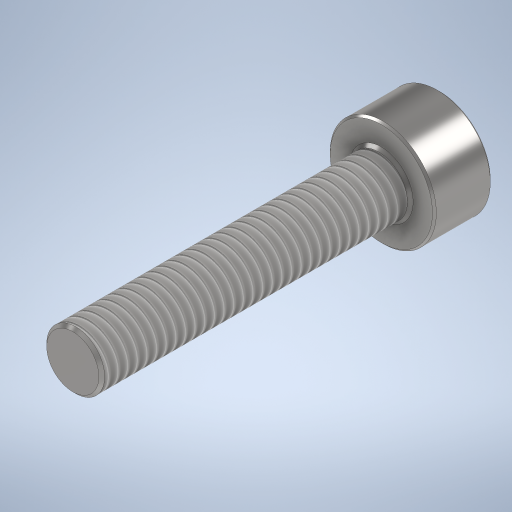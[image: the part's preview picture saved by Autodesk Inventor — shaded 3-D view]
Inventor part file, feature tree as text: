
AUTODESK INVENTOR PART (.ipt)
format: ipt  version: 2024 (Build 280153000, 153)  size: 331,264 bytes
history: native  units: mm
features: extrude x3, chamfer x3, sketch x2, thread x1, hole x1
ambient origin geometry x8: Origin, YZ Plane, XZ Plane, XY Plane, X Axis, Y Axis, Z Axis, Center Point
bodies: Solid1 (feature_tree)
feature tree (10):
  sketch  "Sketch1"  dims[d0=5.5mm d1=3.0mm]
  extrude  "Extrusion1"  Depth=3.0mm
  extrude  "Extrusion2"  Depth=1.5mm TaperAngle=0.0deg
  thread  "Thread1"  [1 undecoded]
  chamfer  "Chamfer1"  Distance=2.5mm
  sketch  "Sketch2"  dims[d2=16.0mm d3=0.0mm d4=3.0mm d5=0.0mm d6=16.0mm d7=0.0mm d8=0.1mm d9=2.0mm d10=45.0deg d11=2.4mm d12=2.5mm d15=0.35mm d16=2.0mm d17=45.0deg d18=3.0mm d19=0.0mm d20=0.15mm d21=2.0mm d22=45.0deg d23=2.4mm d24=6.0mm d25=4.0mm d26=2.0mm d27=90.0deg d28=1.5mm d29=150.0deg]
  hole  "Hole1"  [1 undecoded]
  chamfer  "Chamfer2"  Distance=3.0mm
  extrude  "Extrusion4"  Depth=1.5mm TaperAngle=45.0deg
  chamfer  "Chamfer3"  Distance=2.4mm
note: 2 required parameter values undecoded (feature->parameter linkage not recoverable at this tier; creation-order binding heuristic only, values carry confidence <= 0.55)
